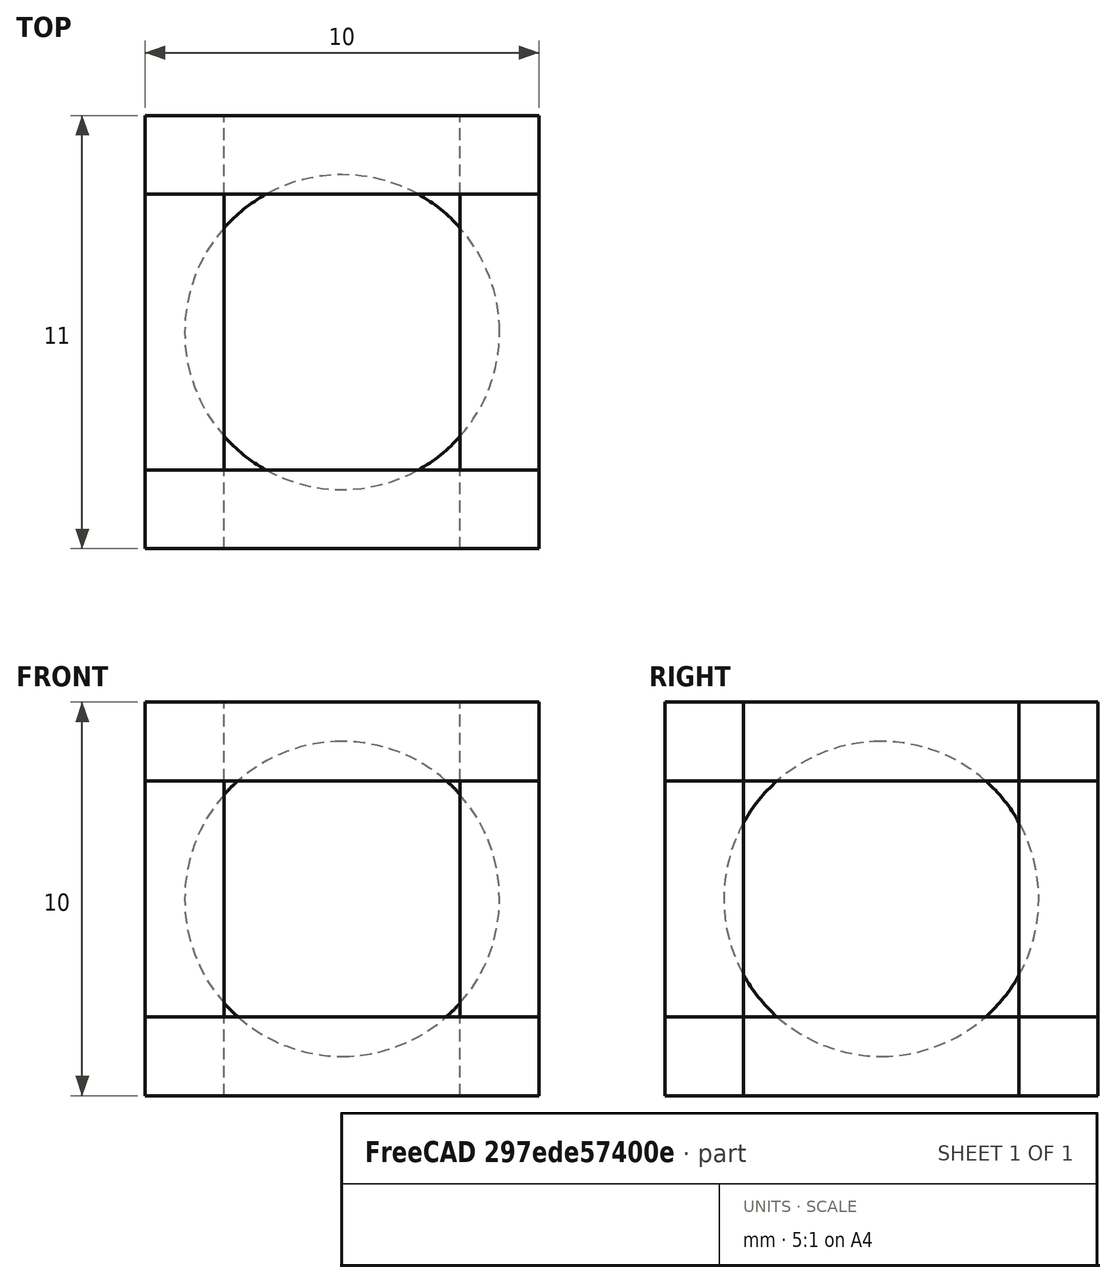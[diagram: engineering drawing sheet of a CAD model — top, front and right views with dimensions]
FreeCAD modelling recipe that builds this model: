
FCSTD DOCUMENT  (FreeCAD 1.0R39109 (Git))
Label: Basic-Cube
License: All rights reserved
LicenseURL: https://en.wikipedia.org/wiki/All_rights_reserved
objects: Part::Box×12, Part::Sphere×1
note: 13 computed .brp shape members not serialized (recipe doc carries the construction recipe); baked Part::Feature solids carry a one-line shape summary decoded from their .brp

FEATURE [Part::Sphere] Sphere
  Angle1 = -90
  Angle2 = 90
  Angle3 = 360
  AttacherType = Attacher::AttachEngine3D
  Placement = pos=(5,5.5,5) rot=(0,0,1;0rad)
  Radius = 4
FEATURE [Part::Box] Box  label="Cube"
  AttacherType = Attacher::AttachEngine3D
  Height = 2
  Length = 2
  Placement = pos=(0,2,0) rot=(0,0,1;0rad)
  Width = 7
FEATURE [Part::Box] Box007  label="Cube001"
  AttacherType = Attacher::AttachEngine3D
  Height = 2
  Length = 2
  Placement = pos=(0,2,8) rot=(0,0,1;0rad)
  Width = 7
FEATURE [Part::Box] Box008  label="Cube002"
  AttacherType = Attacher::AttachEngine3D
  Height = 2
  Length = 2
  Placement = pos=(8,2,0) rot=(0,0,1;0rad)
  Width = 7
FEATURE [Part::Box] Box009  label="Cube003"
  AttacherType = Attacher::AttachEngine3D
  Height = 2
  Length = 2
  Placement = pos=(8,2,8) rot=(0,0,1;0rad)
  Width = 7
FEATURE [Part::Box] Box010  label="Cube004"
  AttacherType = Attacher::AttachEngine3D
  Height = 2
  Length = 10
  Width = 2
FEATURE [Part::Box] Box011  label="Cube005"
  AttacherType = Attacher::AttachEngine3D
  Height = 2
  Length = 10
  Placement = pos=(0,9,0) rot=(0,0,1;0rad)
  Width = 2
FEATURE [Part::Box] Box012  label="Cube006"
  AttacherType = Attacher::AttachEngine3D
  Height = 2
  Length = 10
  Placement = pos=(0,9,8) rot=(0,0,1;0rad)
  Width = 2
FEATURE [Part::Box] Box013  label="Cube007"
  AttacherType = Attacher::AttachEngine3D
  Height = 2
  Length = 10
  Placement = pos=(0,0,8) rot=(0,0,1;0rad)
  Width = 2
FEATURE [Part::Box] Box014  label="Cube008"
  AttacherType = Attacher::AttachEngine3D
  Height = 6
  Length = 2
  Placement = pos=(0,0,2) rot=(0,0,1;0rad)
  Width = 2
FEATURE [Part::Box] Box015  label="Cube009"
  AttacherType = Attacher::AttachEngine3D
  Height = 6
  Length = 2
  Placement = pos=(0,9,2) rot=(0,0,1;0rad)
  Width = 2
FEATURE [Part::Box] Box016  label="Cube010"
  AttacherType = Attacher::AttachEngine3D
  Height = 6
  Length = 2
  Placement = pos=(8,0,2) rot=(0,0,1;0rad)
  Width = 2
FEATURE [Part::Box] Box017  label="Cube011"
  AttacherType = Attacher::AttachEngine3D
  Height = 6
  Length = 2
  Placement = pos=(8,9,2) rot=(0,0,1;0rad)
  Width = 2
